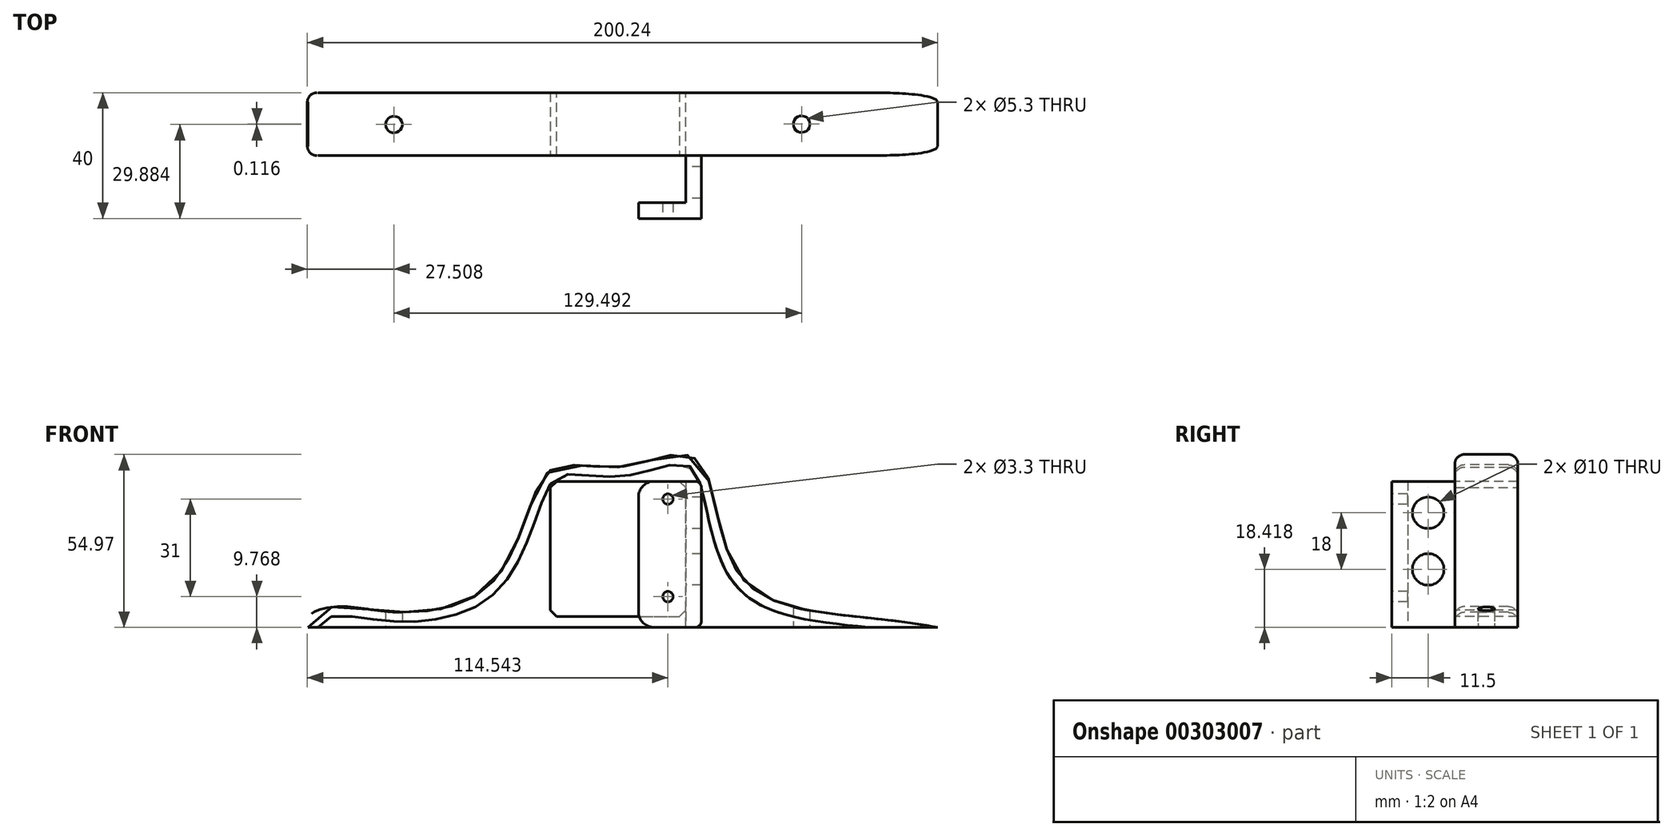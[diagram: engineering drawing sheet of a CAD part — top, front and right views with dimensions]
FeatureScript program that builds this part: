
annotation { "Feature Type Name" : "Feature", "Feature Type Description" : "" }
export const myFeature = defineFeature(function(context is Context, id is Id, definition is map)
    precondition{}
    {
        {
            var Q0;
            Q0=qCreatedBy(makeId("Front.planeOp"),FACE);
            var sketch = newSketch(context, id + "F0", { "sketchPlane" : qUnion([Q0])});
            skLineSegment(sketch, "E0.bottom", {"start": v(21.5, 21.5) * mm, "end": v(-21.5, 21.5) * mm, "construction": true});
            skLineSegment(sketch, "E0.top", {"start": v(21.5, -21.5) * mm, "end": v(-21.5, -21.5) * mm, "construction": true});
            skLineSegment(sketch, "E0.left", {"start": v(21.5, 21.5) * mm, "end": v(21.5, -21.5) * mm, "construction": true});
            skLineSegment(sketch, "E0.right", {"start": v(-21.5, 21.5) * mm, "end": v(-21.5, -21.5) * mm, "construction": true});
            skPoint(sketch, "E0.middle", {"position": v(0, 0) * mm});
            skLineSegment(sketch, "E1", {"start": v(-101.6, -26.5) * mm, "end": v(98.4, -26.5) * mm});
            skLineSegment(sketch, "E2", {"start": v(-109.35, -21.5) * mm, "end": v(107.21, -21.5) * mm, "construction": true});
            skFitSpline(sketch, "E3", {"points": [v(-101.6, -26.5) * mm, v(-92.34, -19.92) * mm, v(-76.2, -21.5) * mm, v(-44.42, -13.53) * mm, v(-28.44, 18.42) * mm, v(-20.7, 24.98) * mm, v(-2.88, 24.47) * mm, v(14.6, 28.34) * mm, v(24.02, 24.3) * mm, v(36.8, -11.52) * mm, v(98.4, -26.5) * mm], "startDerivative": vector(-64.79, 214.02) * mm, "endDerivative": vector(463.93, -90.55) * mm});
            skSolve(sketch);
        }
        {
            var Q0;
            Q0=makeQuery(id+"F0.imprint","IMPRINT",FACE,{"disambiguationData":[TD([[makeQuery(id+"F0.imprint","IMPRINT",EDGE,{"derivedFrom":sQuery(id+"F0.wireOp",EDGE,"E1")}),1.0]])]});
            extrude(context, id + "F1", {"entities" : qUnion([Q0]), "depth" : 20 * mm});
        }
        {
            var Q0;
            Q0=makeQuery(id+"F1.opExtrude","CAP_FACE",FACE,{"disambiguationData":[OSD([sQuery(id+"F0.wireOp",EDGE,"E1"),sQuery(id+"F0.wireOp",EDGE,"E3")])],"isStart":false});
            var sketch = newSketch(context, id + "F2", { "sketchPlane" : qUnion([Q0])});
            skPoint(sketch, "E4.middle", {"position": v(0, 0) * mm});
            skLineSegment(sketch, "E5.bottom", {"start": v(-24.64, -23.08) * mm, "end": v(18.36, -23.08) * mm});
            skLineSegment(sketch, "E5.top", {"start": v(-24.64, 19.92) * mm, "end": v(18.36, 19.92) * mm});
            skLineSegment(sketch, "E5.left", {"start": v(-24.64, -23.08) * mm, "end": v(-24.64, 19.92) * mm});
            skLineSegment(sketch, "E5.right", {"start": v(18.36, -23.08) * mm, "end": v(18.36, 19.92) * mm});
            skSolve(sketch);
        }
        {
            var Q0;
            Q0=makeQuery(id+"F2.imprint","IMPRINT",FACE,{"disambiguationData":[TD([[makeQuery(id+"F2.imprint","IMPRINT",EDGE,{"derivedFrom":sQuery(id+"F2.wireOp",EDGE,"E5.bottom")}),1.0]])]});
            extrude(context, id + "F3", {"entities" : qUnion([Q0]), "operationType" : NewBodyOperationType.REMOVE, "oppositeDirection" : true, "depth" : 21 * mm});
        }
        {
            var Q0;
            Q0=makeQuery(id+"F1.opExtrude","CAP_FACE",FACE,{"disambiguationData":[OSD([sQuery(id+"F0.wireOp",EDGE,"E1"),sQuery(id+"F0.wireOp",EDGE,"E3")])],"isStart":false});
            var sketch = newSketch(context, id + "F4", { "sketchPlane" : qUnion([Q0])});
            skLineSegment(sketch, "E6.bottom", {"start": v(18.36, 19.92) * mm, "end": v(23.36, 19.92) * mm});
            skLineSegment(sketch, "E6.top", {"start": v(18.36, -26.5) * mm, "end": v(23.36, -26.5) * mm});
            skLineSegment(sketch, "E6.left", {"start": v(18.36, 19.92) * mm, "end": v(18.36, -26.5) * mm});
            skLineSegment(sketch, "E6.right", {"start": v(23.36, 19.92) * mm, "end": v(23.36, -26.5) * mm});
            skSolve(sketch);
        }
        {
            var Q0;
            {var subQ3=sQuery(id+"F4.wireOp",EDGE,"E6.bottom");Q0=makeQuery(id+"F4.imprint","IMPRINT",FACE,{"disambiguationData":[TD([[makeQuery(id+"F4.imprint","IMPRINT",EDGE,{"derivedFrom":subQ3}),-1.0]])]});}
            extrude(context, id + "F5", {"entities" : qUnion([Q0]), "operationType" : NewBodyOperationType.ADD, "depth" : 20 * mm});
        }
        {
            var Q0;
            Q0=makeQuery(id+"F1.opExtrude","CAP_EDGE",EDGE,{"disambiguationData":[OSD([sQuery(id+"F0.wireOp",EDGE,"E3")])],"isStart":false});
            var Q1;
            Q1=makeQuery(id+"F1.opExtrude","CAP_EDGE",EDGE,{"disambiguationData":[OSD([sQuery(id+"F0.wireOp",EDGE,"E3")])],"isStart":true});
            fillet(context, id + "F6", {"entities" : qUnion([Q0, Q1]), "radius" : 3 * mm, "tangentPropagation" : true, "allowEdgeOverflow" : false});
        }
        {
            var Q0;
            Q0=makeQuery(id+"F5.opExtrude","SWEPT_EDGE",EDGE,{"disambiguationData":[OSD([sQuery(id+"F4.wireOp",EDGE,"E6.bottom"),sQuery(id+"F4.wireOp",EDGE,"E6.right")])]});
            fillet(context, id + "F7", {"entities" : qUnion([Q0]), "radius" : 2 * mm, "tangentPropagation" : true, "allowEdgeOverflow" : false});
        }
        {
            var Q0;
            Q0=makeQuery(id+"F5.opExtrude","SWEPT_EDGE",EDGE,{"disambiguationData":[OSD([sQuery(id+"F0.wireOp",EDGE,"E1"),sQuery(id+"F4.wireOp",EDGE,"E6.top"),sQuery(id+"F4.wireOp",EDGE,"E6.right")])]});
            fillet(context, id + "F8", {"entities" : qUnion([Q0]), "radius" : 2 * mm, "tangentPropagation" : true, "allowEdgeOverflow" : false});
        }
        {
            var Q0;
            Q0=makeQuery(id+"F5.boolean.opBoolean","MERGE",FACE,{"derivedFrom":[makeQuery(id+"F3.boolean.opBoolean","COPY",FACE,{"derivedFrom":makeQuery(id+"F3.opExtrude","SWEPT_FACE",FACE,{"disambiguationData":[OSD([sQuery(id+"F2.wireOp",EDGE,"E5.right")])]})}),makeQuery(id+"F5.opExtrude","SWEPT_FACE",FACE,{"disambiguationData":[OSD([sQuery(id+"F4.wireOp",EDGE,"E6.left")])]})]});
            var sketch = newSketch(context, id + "F9", { "sketchPlane" : qUnion([Q0])});
            skLineSegment(sketch, "E7.bottom", {"start": v(40, 19.92) * mm, "end": v(35, 19.92) * mm});
            skLineSegment(sketch, "E7.top", {"start": v(40, -26.5) * mm, "end": v(35, -26.5) * mm});
            skLineSegment(sketch, "E7.left", {"start": v(40, 19.92) * mm, "end": v(40, -26.5) * mm});
            skLineSegment(sketch, "E7.right", {"start": v(35, 19.92) * mm, "end": v(35, -26.5) * mm});
            skSolve(sketch);
        }
        {
            var Q0;
            Q0=makeQuery(id+"F9.imprint","IMPRINT",FACE,{"disambiguationData":[TD([[makeQuery(id+"F9.imprint","IMPRINT",EDGE,{"derivedFrom":sQuery(id+"F9.wireOp",EDGE,"E7.bottom")}),1.0]])]});
            extrude(context, id + "F10", {"entities" : qUnion([Q0]), "operationType" : NewBodyOperationType.ADD, "depth" : 15 * mm});
        }
        {
            var Q0;
            Q0=makeQuery(id+"F10.opExtrude","CAP_EDGE",EDGE,{"disambiguationData":[OSD([sQuery(id+"F9.wireOp",EDGE,"E7.top")])],"isStart":false});
            var Q1;
            Q1=makeQuery(id+"F10.opExtrude","CAP_EDGE",EDGE,{"disambiguationData":[OSD([sQuery(id+"F9.wireOp",EDGE,"E7.bottom")])],"isStart":false});
            fillet(context, id + "F11", {"entities" : qUnion([Q0, Q1]), "radius" : 5 * mm, "tangentPropagation" : true, "allowEdgeOverflow" : false});
        }
        {
            var Q0;
            Q0=makeQuery(id+"F3.boolean.opBoolean","COPY",EDGE,{"derivedFrom":makeQuery(id+"F3.opExtrude","SWEPT_EDGE",EDGE,{"disambiguationData":[OSD([sQuery(id+"F2.wireOp",EDGE,"E5.top"),sQuery(id+"F2.wireOp",EDGE,"E5.left")])]})});
            var Q1;
            Q1=makeQuery(id+"F3.boolean.opBoolean","COPY",EDGE,{"derivedFrom":makeQuery(id+"F3.opExtrude","SWEPT_EDGE",EDGE,{"disambiguationData":[OSD([sQuery(id+"F2.wireOp",EDGE,"E5.top"),sQuery(id+"F2.wireOp",EDGE,"E5.right")])]})});
            var Q2;
            Q2=makeQuery(id+"F3.boolean.opBoolean","COPY",EDGE,{"derivedFrom":makeQuery(id+"F3.opExtrude","SWEPT_EDGE",EDGE,{"disambiguationData":[OSD([sQuery(id+"F2.wireOp",EDGE,"E5.bottom"),sQuery(id+"F2.wireOp",EDGE,"E5.left")])]})});
            var Q3;
            Q3=makeQuery(id+"F3.boolean.opBoolean","COPY",EDGE,{"derivedFrom":makeQuery(id+"F3.opExtrude","SWEPT_EDGE",EDGE,{"disambiguationData":[OSD([sQuery(id+"F2.wireOp",EDGE,"E5.bottom"),sQuery(id+"F2.wireOp",EDGE,"E5.right")])]})});
            chamfer(context, id + "F12", {"entities" : qUnion([Q0, Q1, Q2, Q3]), "width" : 2 * mm, "tangentPropagation" : true});
        }
        {
            var Q0;
            Q0=makeQuery(id+"F10.boolean.opBoolean","MERGE",FACE,{"derivedFrom":[makeQuery(id+"F5.opExtrude","CAP_FACE",FACE,{"disambiguationData":[OSD([sQuery(id+"F4.wireOp",EDGE,"E6.bottom"),sQuery(id+"F4.wireOp",EDGE,"E6.top"),sQuery(id+"F4.wireOp",EDGE,"E6.left"),sQuery(id+"F4.wireOp",EDGE,"E6.right")])],"isStart":false}),makeQuery(id+"F10.opExtrude","SWEPT_FACE",FACE,{"disambiguationData":[OSD([sQuery(id+"F9.wireOp",EDGE,"E7.left")])]})]});
            var sketch = newSketch(context, id + "F13", { "sketchPlane" : qUnion([Q0])});
            skLineSegment(sketch, "E8", {"start": v(23.36, 14.27) * mm, "end": v(12.71, 14.27) * mm, "construction": true});
            skCircle(sketch, "E9", {"center": v(12.71, 14.27) * mm, "radius": 1.65 * mm});
            skLineSegment(sketch, "E10", {"start": v(12.71, 14.27) * mm, "end": v(12.71, -16.73) * mm, "construction": true});
            skCircle(sketch, "E11", {"center": v(12.71, -16.73) * mm, "radius": 1.65 * mm});
            skSolve(sketch);
        }
        {
            var Q0;
            Q0=makeQuery(id+"F13.imprint","IMPRINT",FACE,{"disambiguationData":[TD([[makeQuery(id+"F13.imprint","IMPRINT",EDGE,{"derivedFrom":sQuery(id+"F13.wireOp",EDGE,"E11")}),1.0]])]});
            var Q1;
            Q1=makeQuery(id+"F13.imprint","IMPRINT",FACE,{"disambiguationData":[TD([[makeQuery(id+"F13.imprint","IMPRINT",EDGE,{"derivedFrom":sQuery(id+"F13.wireOp",EDGE,"E9")}),1.0]])]});
            extrude(context, id + "F14", {"entities" : qUnion([Q0, Q1]), "operationType" : NewBodyOperationType.REMOVE, "oppositeDirection" : true, "depth" : 10 * mm});
        }
        {
            var Q0;
            Q0=makeQuery(id+"F10.boolean.opBoolean","MERGE",FACE,{"derivedFrom":[makeQuery(id+"F5.boolean.opBoolean","MERGE",FACE,{"derivedFrom":[makeQuery(id+"F1.opExtrude","SWEPT_FACE",FACE,{"disambiguationData":[OSD([sQuery(id+"F0.wireOp",EDGE,"E1")])]}),makeQuery(id+"F5.opExtrude","SWEPT_FACE",FACE,{"disambiguationData":[OSD([sQuery(id+"F4.wireOp",EDGE,"E6.top")])]})]}),makeQuery(id+"F10.opExtrude","SWEPT_FACE",FACE,{"disambiguationData":[OSD([sQuery(id+"F9.wireOp",EDGE,"E7.top")])]})]});
            var sketch = newSketch(context, id + "F15", { "sketchPlane" : qUnion([Q0])});
            skLineSegment(sketch, "E12", {"start": v(-115.33, 10) * mm, "end": v(113.61, 10) * mm, "construction": true});
            skPoint(sketch, "E12.startSnap0", {"position": v(-101.6, 10) * mm});
            skCircle(sketch, "E13", {"center": v(55.17, 10) * mm, "radius": 2.65 * mm});
            skSolve(sketch);
        }
        {
            var Q0;
            Q0=makeQuery(id+"F15.imprint","IMPRINT",FACE,{"disambiguationData":[TD([[makeQuery(id+"F15.imprint","IMPRINT",EDGE,{"derivedFrom":sQuery(id+"F15.wireOp",EDGE,"E13")}),1.0]])]});
            extrude(context, id + "F16", {"entities" : qUnion([Q0]), "operationType" : NewBodyOperationType.REMOVE, "oppositeDirection" : true, "depth" : 25 * mm});
        }
        {
            var Q0;
            Q0=makeQuery(id+"F15.imprint","IMPRINT",FACE,{"disambiguationData":[TD([[makeQuery(id+"F15.imprint","IMPRINT",EDGE,{"derivedFrom":sQuery(id+"F15.wireOp",EDGE,"E13")}),-1.0]])]});
            var sketch = newSketch(context, id + "F17", { "sketchPlane" : qUnion([Q0])});
            skCircle(sketch, "E14", {"center": v(-74.32, 10.12) * mm, "radius": 2.65 * mm});
            skSolve(sketch);
        }
        {
            var Q0;
            Q0=makeQuery(id+"F17.imprint","IMPRINT",FACE,{"disambiguationData":[TD([[makeQuery(id+"F17.imprint","IMPRINT",EDGE,{"derivedFrom":sQuery(id+"F17.wireOp",EDGE,"E14")}),1.0]])]});
            extrude(context, id + "F18", {"entities" : qUnion([Q0]), "operationType" : NewBodyOperationType.REMOVE, "oppositeDirection" : true, "depth" : 25 * mm});
        }
        {
            var Q0;
            Q0=makeQuery(id+"F5.boolean.opBoolean","MERGE",FACE,{"derivedFrom":[makeQuery(id+"F3.boolean.opBoolean","COPY",FACE,{"derivedFrom":makeQuery(id+"F3.opExtrude","SWEPT_FACE",FACE,{"disambiguationData":[OSD([sQuery(id+"F2.wireOp",EDGE,"E5.right")])]})}),makeQuery(id+"F5.opExtrude","SWEPT_FACE",FACE,{"disambiguationData":[OSD([sQuery(id+"F4.wireOp",EDGE,"E6.left")])]})]});
            var sketch = newSketch(context, id + "F19", { "sketchPlane" : qUnion([Q0])});
            skLineSegment(sketch, "E15", {"start": v(35, 9.92) * mm, "end": v(28.5, 9.92) * mm, "construction": true});
            skCircle(sketch, "E16", {"center": v(28.5, 9.92) * mm, "radius": 5 * mm});
            skLineSegment(sketch, "E17", {"start": v(28.5, 9.92) * mm, "end": v(28.5, -8.08) * mm, "construction": true});
            skCircle(sketch, "E18", {"center": v(28.5, -8.08) * mm, "radius": 5 * mm});
            skSolve(sketch);
        }
        {
            var Q0;
            Q0=makeQuery(id+"F19.imprint","IMPRINT",FACE,{"disambiguationData":[TD([[makeQuery(id+"F19.imprint","IMPRINT",EDGE,{"derivedFrom":sQuery(id+"F19.wireOp",EDGE,"E18")}),1.0]])]});
            var Q1;
            Q1=makeQuery(id+"F19.imprint","IMPRINT",FACE,{"disambiguationData":[TD([[makeQuery(id+"F19.imprint","IMPRINT",EDGE,{"derivedFrom":sQuery(id+"F19.wireOp",EDGE,"E16")}),1.0]])]});
            extrude(context, id + "F20", {"entities" : qUnion([Q0, Q1]), "operationType" : NewBodyOperationType.REMOVE, "oppositeDirection" : true, "depth" : 25 * mm});
        }
    });
